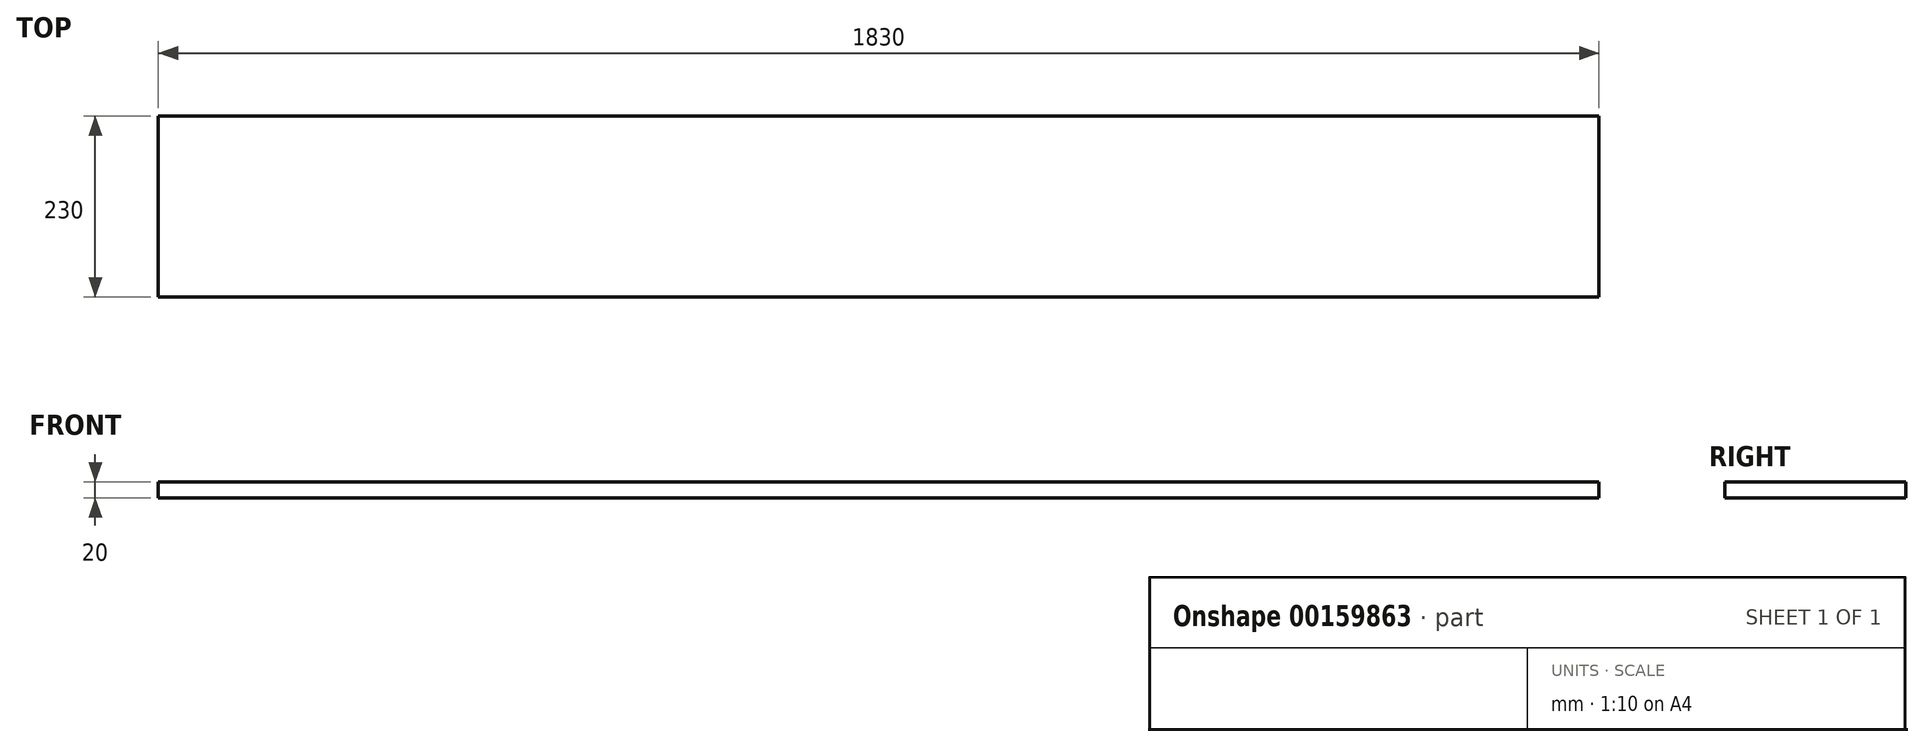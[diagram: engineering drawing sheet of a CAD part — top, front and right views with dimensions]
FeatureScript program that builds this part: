
annotation { "Feature Type Name" : "Feature", "Feature Type Description" : "" }
export const myFeature = defineFeature(function(context is Context, id is Id, definition is map)
    precondition{}
    {
        {
            assignVariable(context, id + "F0", {"name" : "t", "anyValue" : 20 * mm});
        }
        {
            var Q0;
            Q0=qCreatedBy(makeId("Top.planeOp"),FACE);
            var sketch = newSketch(context, id + "F1", { "sketchPlane" : qUnion([Q0])});
            skLineSegment(sketch, "E0.bottom", {"start": v(915, -115) * mm, "end": v(-915, -115) * mm});
            skLineSegment(sketch, "E0.top", {"start": v(915, 115) * mm, "end": v(-915, 115) * mm});
            skLineSegment(sketch, "E0.left", {"start": v(915, -115) * mm, "end": v(915, 115) * mm});
            skLineSegment(sketch, "E0.right", {"start": v(-915, -115) * mm, "end": v(-915, 115) * mm});
            skPoint(sketch, "E0.middle", {"position": v(0, 0) * mm});
            skSolve(sketch);
        }
        {
            var Q0;
            Q0 = qSketchRegion(id + "F1", true);
            extrude(context, id + "F2", {"entities" : qUnion([Q0]), "depth" : getVariable(context, 't')});
        }
    });
